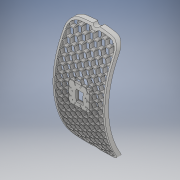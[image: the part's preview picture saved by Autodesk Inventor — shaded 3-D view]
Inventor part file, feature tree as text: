
AUTODESK INVENTOR PART (.ipt)
format: ipt  version: 2019 (Build 230136000, 136)  size: 5,235,712 bytes
history: native  units: mm
features: extrude x9, sketch x7, other x3, projected_geometry x2, pattern_linear x1, plane x1, hole x1
ambient origin geometry x8: Origin, YZ Plane, XZ Plane, XY Plane, X Axis, Y Axis, Z Axis, Center Point
bodies: Volumenkörper2 (feature_tree), Volumenkörper4 (feature_tree), Volumenkörper1 (feature_tree)
feature tree (24):
  other  "Brille_Glas_Zusammenbau.ipt"
  sketch  "Skizze1"  dims[d0=10.0mm d2=1.0mm d3=60.0mm d4=0.0mm]
  sketch  "Skizze3"  dims[d11=250.0mm d13=11.0mm d14=140.0mm d16=11.0mm]
  extrude  "Extrusion1"  Depth=1.0mm
  pattern_linear  "Rechteckige Anordnung2"  Count1=6 Spacing1=0.0mm
  sketch  "Skizze10"  dims[d25=0.5mm d26=3.5mm]
  extrude  "Extrusion5"  Depth=140.0mm
  extrude  "Extrusion6"  Depth=3.5mm
  extrude  "Extrusion7"  Depth=60.0mm TaperAngle=0.0deg
  sketch  "Skizze11"  dims[d27=60.0mm d28=0.0mm d29=60.0mm d30=0.0mm]
  extrude  "Extrusion8"  Depth=25.0mm
  plane  "Arbeitsebene1"
  sketch  "Skizze12"  dims[d31=60.0mm d32=0.0mm d33=25.0mm]
  extrude  "Extrusion9"  TaperAngle=0.0deg  [1 undecoded]
  hole  "Bohrung1"  [1 undecoded]
  extrude  "Extrusion10"  Depth=4.0mm
  extrude  "Extrusion11"  Depth=6.0mm
  extrude  "Extrusion12"  Depth=7.7mm
  other  "Volumenkörper7::Brille_Glas_Zusammenbau.ipt"
  other  "Bezeichnung1"
  projected_geometry  "Projizierte Kontur1"
  sketch  "Skizze13"  dims[d34=24.0mm d35=0.0mm d36=0.0mm]
  sketch  "Skizze14"  dims[d37=42.967mm d40=2.5mm d41=4.0mm d42=6.0mm d43=7.7mm d44=4.6mm d45=0.0mm d46=4.0mm d47=2.0mm d48=3.6mm d49=0.0mm d50=0.0mm d51=0.0mm d52=2.0mm d53=2.0mm d54=2.0mm d55=2.0mm d56=12.5mm d57=2.0mm d58=2.0mm d59=12.5mm d60=1.5mm d61=6.0mm d62=4.0mm d63=2.0mm d64=90.0deg d65=30.0mm d66=0.0mm d67=4.0mm d68=0.0mm]
  projected_geometry  "Projizierte Kontur6"
note: 2 required parameter values undecoded (feature->parameter linkage not recoverable at this tier; creation-order binding heuristic only, values carry confidence <= 0.55)
